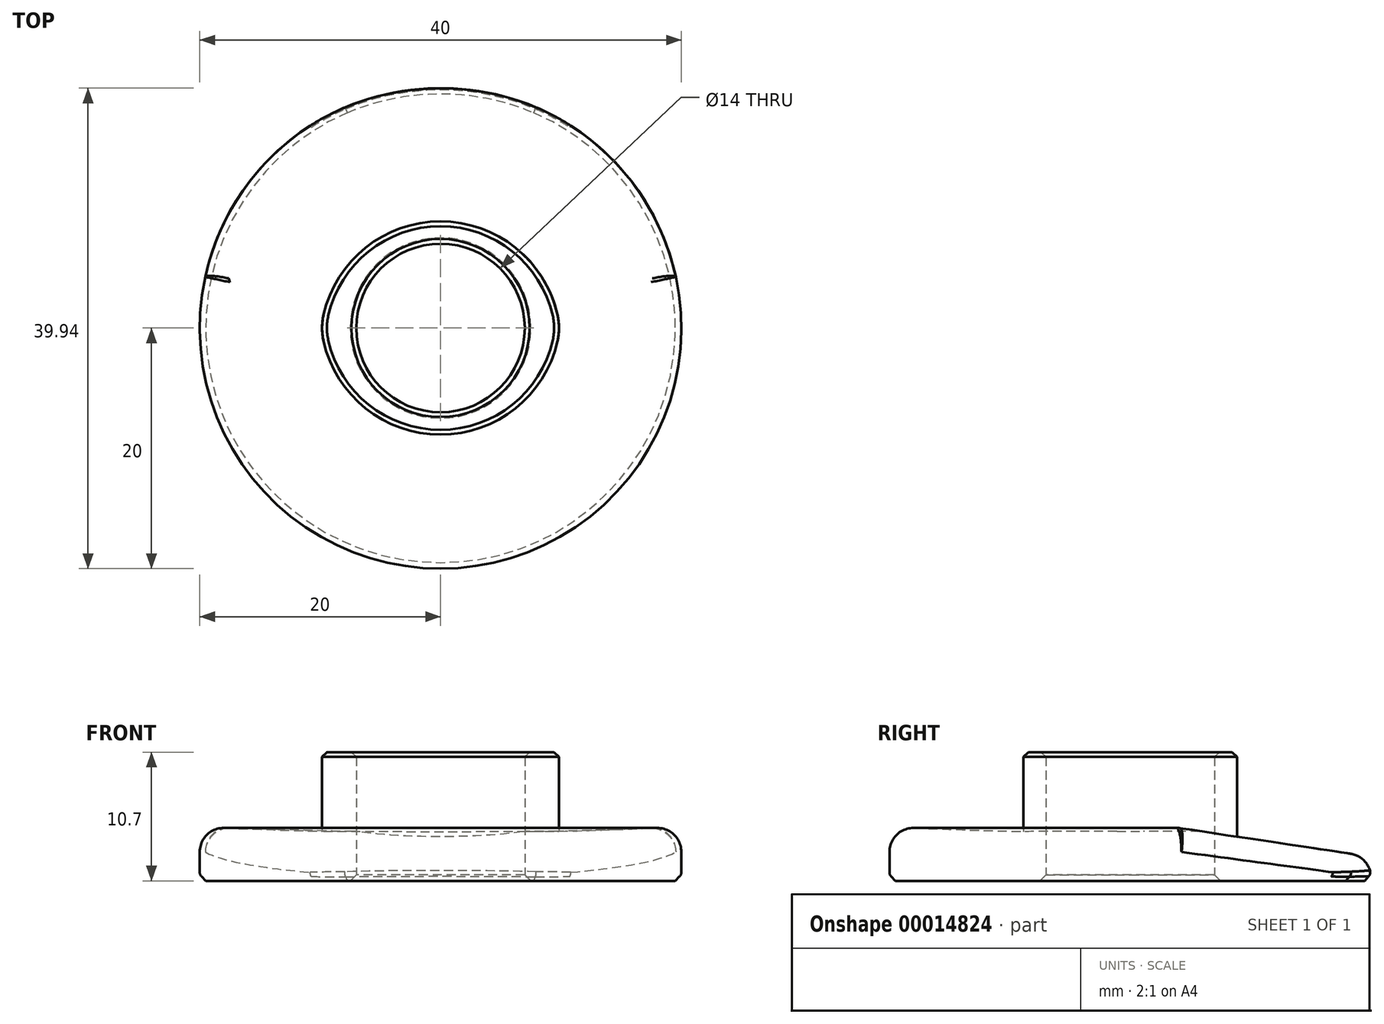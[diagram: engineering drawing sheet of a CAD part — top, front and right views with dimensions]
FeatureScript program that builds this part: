
annotation { "Feature Type Name" : "Feature", "Feature Type Description" : "" }
export const myFeature = defineFeature(function(context is Context, id is Id, definition is map)
    precondition{}
    {
        {
            var Q0;
            Q0=qCreatedBy(makeId("Top.planeOp"),FACE);
            var sketch = newSketch(context, id + "F0", { "sketchPlane" : qUnion([Q0])});
            skCircle(sketch, "E0", {"center": v(0, 0) * mm, "radius": 20 * mm});
            skArc(sketch, "E1", {"start": v(9.9, 0) * mm, "mid": v(0, 8.86) * mm, "end": v(-9.9, 0) * mm});
            skArc(sketch, "E2", {"start": v(-9.9, 0) * mm, "mid": v(0, -8.86) * mm, "end": v(9.9, 0) * mm});
            skLineSegment(sketch, "E3", {"start": v(-9.9, 0) * mm, "end": v(9.9, 0) * mm, "construction": true});
            skCircle(sketch, "E4", {"center": v(0, 0) * mm, "radius": 7 * mm});
            skSolve(sketch);
        }
        {
            var Q0;
            Q0 = qSketchRegion(id + "F0", true);
            extrude(context, id + "F1", {"entities" : qUnion([Q0]), "depth" : 5 * mm});
        }
        {
            var Q0;
            Q0=qCreatedBy(makeId("Right.planeOp"),FACE);
            var sketch = newSketch(context, id + "F2", { "sketchPlane" : qUnion([Q0])});
            skLineSegment(sketch, "E5", {"start": v(0, 5) * mm, "end": v(20, 5) * mm});
            skLineSegment(sketch, "E6", {"start": v(20, 2) * mm, "end": v(0, 5) * mm});
            skLineSegment(sketch, "E7", {"start": v(20, 2) * mm, "end": v(20, 5) * mm});
            skSolve(sketch);
        }
        {
            var Q0;
            Q0 = qSketchRegion(id + "F2", true);
            extrude(context, id + "F3", {"entities" : qUnion([Q0]), "operationType" : NewBodyOperationType.REMOVE, "endBound" : BoundingType.THROUGH_ALL, "oppositeDirection" : true, "depth" : 25 * mm, "hasSecondDirection" : true, "secondDirectionBound" : BoundingType.THROUGH_ALL, "secondDirectionOppositeDirection" : false, "secondDirectionDepth" : 25 * mm});
        }
        {
            var Q0;
            Q0=qCreatedBy(makeId("Front.planeOp"),FACE);
            var sketch = newSketch(context, id + "F4", { "sketchPlane" : qUnion([Q0])});
            skCircle(sketch, "E8", {"center": v(0, 404) * mm, "radius": 400 * mm, "construction": true});
            skSolve(sketch);
        }
        {
            var Q0;
            Q0=qCreatedBy(makeId("Right.planeOp"),FACE);
            var sketch = newSketch(context, id + "F5", { "sketchPlane" : qUnion([Q0])});
            skArc(sketch, "E9", {"start": v(100, 791.3) * mm, "mid": v(0, 804) * mm, "end": v(-100, 791.3) * mm});
            skLineSegment(sketch, "E10", {"start": v(100, 791.3) * mm, "end": v(-100, 791.3) * mm});
            skSolve(sketch);
        }
        {
            var Q0;
            Q0 = qSketchRegion(id + "F5", true);
            var Q1;
            Q1=sQuery(id+"F4.wireOp",EDGE,"E8");
            revolve(context, id + "F6", {"operationType" : NewBodyOperationType.REMOVE, "entities" : qUnion([Q0]), "axis" : qUnion([Q1]), "revolveType" : RevolveType.FULL, "oppositeDirection" : true});
        }
        {
            var Q0;
            Q0=makeQuery(id+"F3.boolean.opBoolean","INTERSECT",EDGE,{"derivedFrom":[makeQuery(id+"F1.opExtrude","SWEPT_FACE",FACE,{"disambiguationData":[OSD([sQuery(id+"F0.wireOp",EDGE,"E0")])]}),makeQuery(id+"F3.opExtrude","SWEPT_FACE",FACE,{"disambiguationData":[OSD([sQuery(id+"F2.wireOp",EDGE,"E6")])]})]});
            var Q1;
            Q1=makeQuery(id+"F1.opExtrude","CAP_EDGE",EDGE,{"disambiguationData":[OSD([sQuery(id+"F0.wireOp",EDGE,"E0")])],"isStart":false});
            fillet(context, id + "F7", {"entities" : qUnion([Q0, Q1]), "radius" : 2 * mm, "tangentPropagation" : true, "allowEdgeOverflow" : false});
        }
        {
            var Q0;
            Q0=makeQuery(id+"F6.boolean.opBoolean","INTERSECT",EDGE,{"disambiguationData":[OD(1.0)],"derivedFrom":[makeQuery(id+"F3.boolean.opBoolean","COPY",FACE,{"derivedFrom":makeQuery(id+"F3.opExtrude","SWEPT_FACE",FACE,{"disambiguationData":[OSD([sQuery(id+"F2.wireOp",EDGE,"E6")])]})}),makeQuery(id+"F6.opRevolve","SWEPT_FACE",FACE,{"disambiguationData":[OSD([sQuery(id+"F5.wireOp",EDGE,"E9")])]})]});
            var Q1;
            Q1=makeQuery(id+"F6.boolean.opBoolean","INTERSECT",EDGE,{"disambiguationData":[OD(0.0)],"derivedFrom":[makeQuery(id+"F3.boolean.opBoolean","COPY",FACE,{"derivedFrom":makeQuery(id+"F3.opExtrude","SWEPT_FACE",FACE,{"disambiguationData":[OSD([sQuery(id+"F2.wireOp",EDGE,"E6")])]})}),makeQuery(id+"F6.opRevolve","SWEPT_FACE",FACE,{"disambiguationData":[OSD([sQuery(id+"F5.wireOp",EDGE,"E9")])]})]});
            fillet(context, id + "F8", {"entities" : qUnion([Q0, Q1]), "radius" : 2 * mm, "tangentPropagation" : true, "allowEdgeOverflow" : false});
        }
        {
            var Q0;
            Q0=makeQuery(id+"F0.imprint","IMPRINT",FACE,{"disambiguationData":[TD([[makeQuery(id+"F0.imprint","IMPRINT",EDGE,{"derivedFrom":sQuery(id+"F0.wireOp",EDGE,"E1")}),1.0]])]});
            extrude(context, id + "F9", {"entities" : qUnion([Q0]), "operationType" : NewBodyOperationType.ADD, "depth" : 10.7 * mm});
        }
        {
            var Q0;
            Q0=makeQuery(id+"F9.opExtrude","CAP_EDGE",EDGE,{"disambiguationData":[OSD([sQuery(id+"F0.wireOp",EDGE,"E4")])],"isStart":true});
            var Q1;
            Q1=makeQuery(id+"F1.opExtrude","CAP_EDGE",EDGE,{"disambiguationData":[OSD([sQuery(id+"F0.wireOp",EDGE,"E0")])],"isStart":true});
            chamfer(context, id + "F10", {"entities" : qUnion([Q0, Q1]), "width" : .5 * mm, "tangentPropagation" : true});
        }
        {
            var Q0;
            {var subQ0=sQuery(id+"F0.wireOp",EDGE,"E1");var subQ1=sQuery(id+"F0.wireOp",EDGE,"E2");Q0=makeQuery(id+"F9.opExtrude","SWEPT_EDGE",EDGE,{"disambiguationData":[OSD([subQ0,subQ1]),TDD([makeQuery(id+"F0.imprint","INTERSECT",VERTEX,{"disambiguationData":[OD(1.0)],"derivedFrom":[subQ0,subQ1]})])]});}
            var Q1;
            {var subQ0=sQuery(id+"F0.wireOp",EDGE,"E1");var subQ1=sQuery(id+"F0.wireOp",EDGE,"E2");Q1=makeQuery(id+"F9.opExtrude","SWEPT_EDGE",EDGE,{"disambiguationData":[OSD([subQ0,subQ1]),TDD([makeQuery(id+"F0.imprint","INTERSECT",VERTEX,{"disambiguationData":[OD(0.0)],"derivedFrom":[subQ0,subQ1]})])]});}
            fillet(context, id + "F11", {"entities" : qUnion([Q0, Q1]), "radius" : 5 * mm, "tangentPropagation" : true, "allowEdgeOverflow" : false});
        }
        {
            var Q0;
            Q0=makeQuery(id+"F9.opExtrude","CAP_FACE",FACE,{"disambiguationData":[OSD([sQuery(id+"F0.wireOp",EDGE,"E1"),sQuery(id+"F0.wireOp",EDGE,"E2"),sQuery(id+"F0.wireOp",EDGE,"E4")])],"isStart":false});
            chamfer(context, id + "F12", {"entities" : qUnion([Q0]), "width" : .4 * mm, "tangentPropagation" : true});
        }
        {
            var Q0;
            {var subQ0=sQuery(id+"F0.wireOp",EDGE,"E0");Q0=makeQuery(id+"F10.opChamfer","BLEND_EDGE",EDGE,{"blendedFrom":[makeQuery(id+"F1.opExtrude","CAP_EDGE",EDGE,{"disambiguationData":[OSD([subQ0])],"isStart":true}),makeQuery(id+"F7.opFillet","BLEND_FACE",FACE,{"disambiguationData":[OSD([subQ0,sQuery(id+"F2.wireOp",EDGE,"E6")])]})],"blendedInto":[makeQuery(id+"F7.opFillet","BLEND_FACE",FACE,{"disambiguationData":[OSD([subQ0,sQuery(id+"F2.wireOp",EDGE,"E6")])]})]});}
            fillet(context, id + "F13", {"entities" : qUnion([Q0]), "radius" : .5 * mm, "tangentPropagation" : true, "allowEdgeOverflow" : false});
        }
    });
